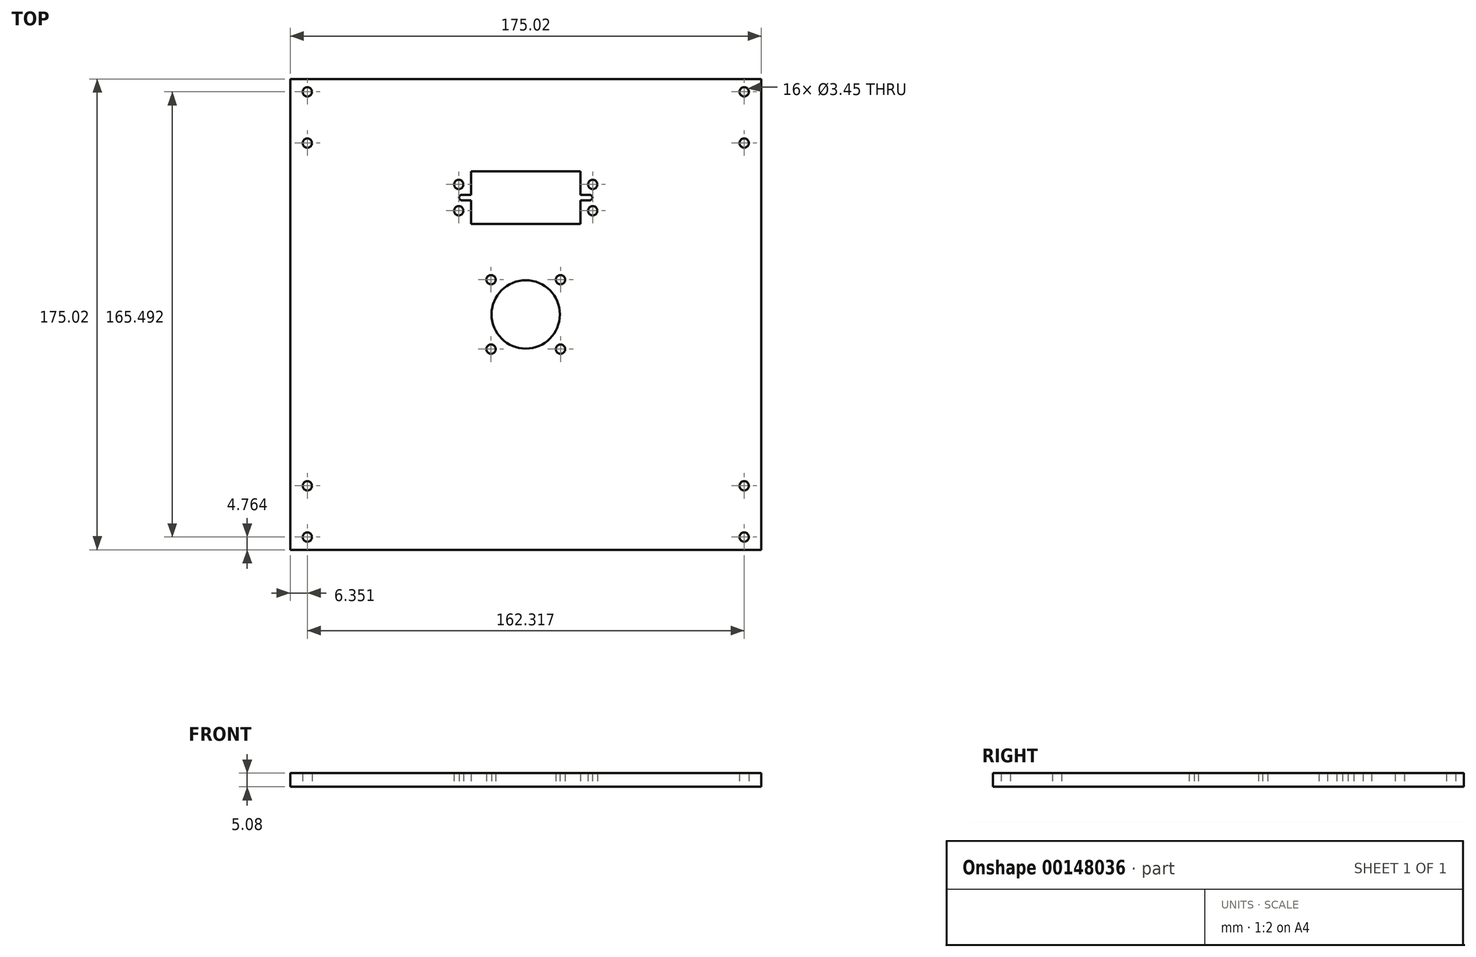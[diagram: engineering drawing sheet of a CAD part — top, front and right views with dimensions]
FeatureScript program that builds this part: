
annotation { "Feature Type Name" : "Feature", "Feature Type Description" : "" }
export const myFeature = defineFeature(function(context is Context, id is Id, definition is map)
    precondition{}
    {
        {
            var Q0;
            Q0=qCreatedBy(makeId("Top.planeOp"),FACE);
            var sketch = newSketch(context, id + "F0", { "sketchPlane" : qUnion([Q0])});
            skLineSegment(sketch, "E0.bottom", {"start": v(-12.9, 12.9) * mm, "end": v(12.9, 12.9) * mm, "construction": true});
            skLineSegment(sketch, "E0.top", {"start": v(-12.9, -12.9) * mm, "end": v(12.9, -12.9) * mm, "construction": true});
            skLineSegment(sketch, "E0.left", {"start": v(-12.9, 12.9) * mm, "end": v(-12.9, -12.9) * mm, "construction": true});
            skLineSegment(sketch, "E0.right", {"start": v(12.9, 12.9) * mm, "end": v(12.9, -12.9) * mm, "construction": true});
            skPoint(sketch, "E0.middle", {"position": v(0, 0) * mm});
            skCircle(sketch, "E1", {"center": v(0, 0) * mm, "radius": 14.29 * mm, "construction": true});
            skCircle(sketch, "E2", {"center": v(-12.9, 12.9) * mm, "radius": 3.97 * mm, "construction": true});
            skCircle(sketch, "E3", {"center": v(-12.9, 12.9) * mm, "radius": 1.73 * mm});
            skCircle(sketch, "E4", {"center": v(12.9, 12.9) * mm, "radius": 1.73 * mm});
            skCircle(sketch, "E5", {"center": v(12.9, -12.9) * mm, "radius": 1.73 * mm});
            skCircle(sketch, "E6", {"center": v(-12.9, -12.9) * mm, "radius": 1.73 * mm});
            skLineSegment(sketch, "E7", {"start": v(0, 0) * mm, "end": v(0, 0) * mm});
            skLineSegment(sketch, "E8.bottom", {"start": v(-87.5, 87.5) * mm, "end": v(87.5, 87.5) * mm});
            skLineSegment(sketch, "E8.top", {"start": v(-87.5, -87.5) * mm, "end": v(87.5, -87.5) * mm});
            skLineSegment(sketch, "E8.left", {"start": v(-87.5, 87.5) * mm, "end": v(-87.5, -87.5) * mm});
            skLineSegment(sketch, "E8.right", {"start": v(87.5, 87.5) * mm, "end": v(87.5, -87.5) * mm});
            skLineSegment(sketch, "E9", {"start": v(-87.5, 82.75) * mm, "end": v(-81.16, 82.75) * mm, "construction": true});
            skLineSegment(sketch, "E10", {"start": v(-81.16, 82.75) * mm, "end": v(-81.16, 87.5) * mm, "construction": true});
            skLineSegment(sketch, "E11", {"start": v(-81.16, -87.5) * mm, "end": v(-81.16, -82.75) * mm, "construction": true});
            skLineSegment(sketch, "E12", {"start": v(-81.16, -82.75) * mm, "end": v(-81.16, -63.7) * mm, "construction": true});
            skLineSegment(sketch, "E13", {"start": v(81.16, 87.5) * mm, "end": v(81.16, 82.75) * mm, "construction": true});
            skLineSegment(sketch, "E14", {"start": v(81.16, 82.75) * mm, "end": v(87.5, 82.75) * mm, "construction": true});
            skLineSegment(sketch, "E15", {"start": v(81.16, 82.75) * mm, "end": v(81.16, 63.7) * mm, "construction": true});
            skLineSegment(sketch, "E16", {"start": v(-81.16, 82.75) * mm, "end": v(-81.16, 63.7) * mm, "construction": true});
            skLineSegment(sketch, "E17", {"start": v(81.16, -87.5) * mm, "end": v(81.16, -82.75) * mm, "construction": true});
            skLineSegment(sketch, "E18", {"start": v(81.16, -82.75) * mm, "end": v(81.16, -63.7) * mm, "construction": true});
            skCircle(sketch, "E19", {"center": v(-81.16, 82.75) * mm, "radius": 1.73 * mm});
            skCircle(sketch, "E20", {"center": v(-81.16, 63.7) * mm, "radius": 1.73 * mm});
            skCircle(sketch, "E21", {"center": v(-81.16, -63.7) * mm, "radius": 1.73 * mm});
            skCircle(sketch, "E22", {"center": v(-81.16, -82.75) * mm, "radius": 1.73 * mm});
            skCircle(sketch, "E23", {"center": v(81.16, -82.75) * mm, "radius": 1.73 * mm});
            skCircle(sketch, "E24", {"center": v(81.16, -63.7) * mm, "radius": 1.73 * mm});
            skCircle(sketch, "E25", {"center": v(81.16, 63.7) * mm, "radius": 1.73 * mm});
            skCircle(sketch, "E26", {"center": v(81.16, 82.75) * mm, "radius": 1.73 * mm});
            skLineSegment(sketch, "E27", {"start": v(0, 0) * mm, "end": v(0, 33.66) * mm, "construction": true});
            skLineSegment(sketch, "E28", {"start": v(0, 33.66) * mm, "end": v(0, 53.22) * mm, "construction": true});
            skLineSegment(sketch, "E29", {"start": v(-20.32, 53.22) * mm, "end": v(20.32, 53.22) * mm});
            skLineSegment(sketch, "E30", {"start": v(-20.32, 33.66) * mm, "end": v(20.32, 33.66) * mm});
            skLineSegment(sketch, "E31", {"start": v(-20.32, 53.22) * mm, "end": v(-20.32, 44.45) * mm});
            skLineSegment(sketch, "E32", {"start": v(-20.32, 33.66) * mm, "end": v(-20.32, 42.42) * mm});
            skLineSegment(sketch, "E33", {"start": v(20.32, 33.66) * mm, "end": v(20.32, 42.42) * mm});
            skLineSegment(sketch, "E34", {"start": v(20.32, 53.22) * mm, "end": v(20.32, 44.45) * mm});
            skLineSegment(sketch, "E35.bottom", {"start": v(20.32, 44.45) * mm, "end": v(23.75, 44.45) * mm});
            skLineSegment(sketch, "E35.top", {"start": v(20.32, 42.42) * mm, "end": v(23.75, 42.42) * mm});
            skLineSegment(sketch, "E35.left", {"start": v(20.32, 44.45) * mm, "end": v(20.32, 42.42) * mm, "construction": true});
            skLineSegment(sketch, "E35.right", {"start": v(23.75, 44.45) * mm, "end": v(23.75, 42.42) * mm, "construction": true});
            skLineSegment(sketch, "E36.bottom", {"start": v(-20.32, 44.45) * mm, "end": v(-23.75, 44.45) * mm});
            skLineSegment(sketch, "E36.top", {"start": v(-20.32, 42.42) * mm, "end": v(-23.75, 42.42) * mm});
            skLineSegment(sketch, "E36.left", {"start": v(-20.32, 44.45) * mm, "end": v(-20.32, 42.42) * mm, "construction": true});
            skLineSegment(sketch, "E36.right", {"start": v(-23.75, 44.45) * mm, "end": v(-23.75, 42.42) * mm, "construction": true});
            skLineSegment(sketch, "E37.bottom", {"start": v(-24.9, 48.33) * mm, "end": v(24.9, 48.33) * mm, "construction": true});
            skLineSegment(sketch, "E37.top", {"start": v(-24.9, 38.55) * mm, "end": v(24.9, 38.55) * mm, "construction": true});
            skLineSegment(sketch, "E37.left", {"start": v(-24.9, 48.33) * mm, "end": v(-24.9, 38.55) * mm, "construction": true});
            skLineSegment(sketch, "E37.right", {"start": v(24.9, 48.33) * mm, "end": v(24.9, 38.55) * mm, "construction": true});
            skPoint(sketch, "E37.middle", {"position": v(0, 43.44) * mm});
            skArc(sketch, "E38", {"start": v(-23.75, 44.45) * mm, "mid": v(-24.77, 43.44) * mm, "end": v(-23.75, 42.42) * mm});
            skArc(sketch, "E39", {"start": v(23.75, 42.42) * mm, "mid": v(24.77, 43.44) * mm, "end": v(23.75, 44.45) * mm});
            skCircle(sketch, "E40", {"center": v(-24.9, 48.33) * mm, "radius": 1.73 * mm});
            skCircle(sketch, "E41", {"center": v(-24.9, 38.55) * mm, "radius": 1.73 * mm});
            skCircle(sketch, "E42", {"center": v(24.9, 38.55) * mm, "radius": 1.73 * mm});
            skCircle(sketch, "E43", {"center": v(24.9, 48.33) * mm, "radius": 1.73 * mm});
            skCircle(sketch, "E44", {"center": v(0, 0) * mm, "radius": 12.7 * mm});
            skLineSegment(sketch, "E45", {"start": v(20.32, 43.44) * mm, "end": v(10.9, 43.44) * mm, "construction": true});
            skLineSegment(sketch, "E46", {"start": v(10.9, 43.44) * mm, "end": v(0, 0) * mm, "construction": true});
            skSolve(sketch);
        }
        {
            var Q0;
            Q0=qSketchRegion(id+"F0",true);
            extrude(context, id + "F1", {"entities" : qUnion([Q0]), "depth" : 5.08 * mm});
        }
    });
